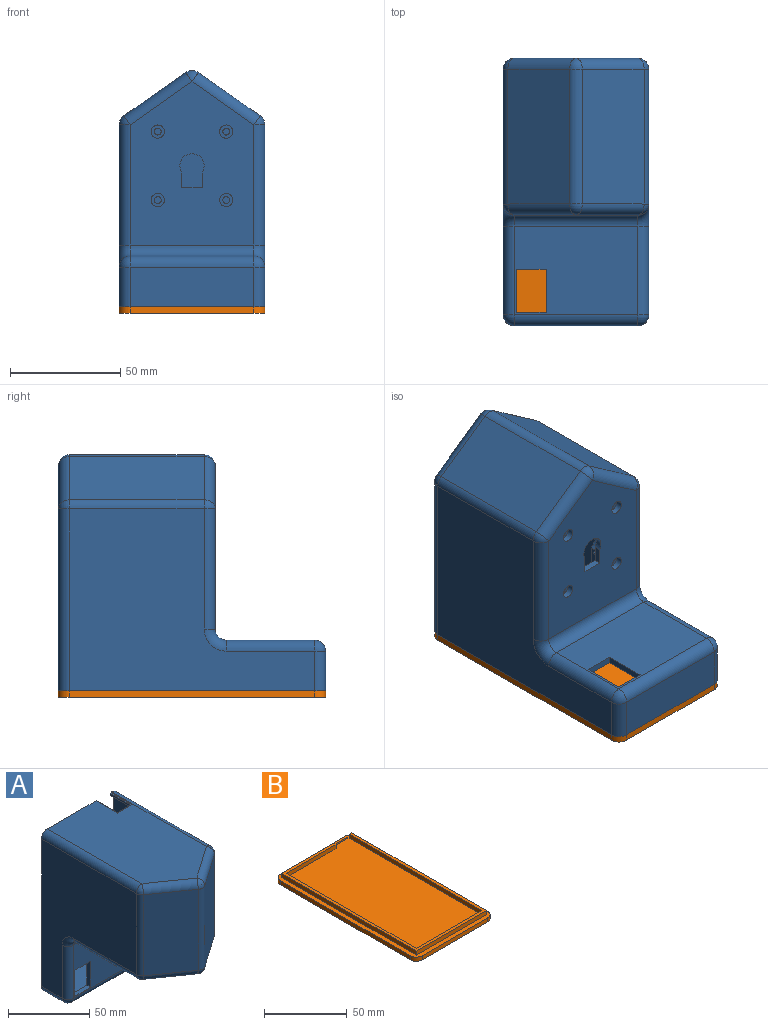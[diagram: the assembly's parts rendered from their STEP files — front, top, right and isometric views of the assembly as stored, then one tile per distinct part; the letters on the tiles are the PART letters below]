
ASSEMBLY  parts=2 mates=1
PART A: 93 faces, bbox 66x107x121 mm
  f0: plane 102x56mm, normal (0,0,1), area 4913.5mm2, adj f1,f3,f17,f56,f57,f63,f64
  f1: plane 13.5x0.75mm, normal (0,1,0), area 10.1mm2, adj f0,f3,f5,f90
  f2: plane 17.5x1.5mm, normal (-1,0,0), area 26.2mm2, adj f17,f89,f90,f92
  f3: plane 18.5x0.75mm, normal (1,0,0), area 13.9mm2, adj f0,f1,f17,f90
  f4: plane 18.5x0.75mm, normal (1,0,0), area 13.9mm2, adj f10,f17,f37,f89
  f5: plane 18.5x0.75mm, normal (-1,0,0), area 13.9mm2, adj f1,f17,f64,f90
  f6: plane 16.5x14.35mm, normal (0,0,1), area 236.8mm2, adj f18,f40,f43,f49
  f7: plane 38x23mm, normal (0,0,1), area 533.9mm2, adj f32,f39,f40,f41,f42,f43,f46,f47
  f8: plane 74x56mm, normal (0,0,-1), area 3336.8mm2, adj f22,f25,f28,f31,f32,f46,f47,f48
  f9: plane 86.01x60mm, normal (0,0,1), area 1780.7mm2, adj f14,f16,f18,f54,f55,f83,f84,f85
  f10: plane 106.01x60mm, normal (0,0,-1), area 5480.4mm2, adj f4,f14,f16,f17,f37,f38,f54,f55
  f11: plane 111x82.4mm, normal (-1,0,0), area 5947.7mm2, adj f17,f56,f60,f68,f69,f70,f74
  f12: plane 56x18mm, normal (0,0,-1), area 1008mm2, adj f17,f68,f76,f77
  f13: plane 111x82.4mm, normal (1,0,0), area 5947.7mm2, adj f17,f64,f72,f76,f79,f81,f82
  f14: plane 115x85mm, normal (-1,0,0), area 6395mm2, adj f9,f10,f15,f17,f18,f55
  f15: plane 60x20mm, normal (0,0,1), area 1200mm2, adj f14,f16,f17,f18
  f16: plane 115x85mm, normal (1,0,0), area 6395mm2, adj f9,f10,f15,f17,f18,f54
  f17: plane 121x66mm, normal (0,1,0), area 1027mm2, adj f0,f2,f3,f4,f5,f10,f11,f12
  f18: plane 60x52mm, normal (0,1,0), area 2823.8mm2, adj f6,f9,f14,f15,f16,f33,f34,f35
  f19: plane 56x40mm, normal (0,-1,0), area 1976.7mm2, adj f33,f34,f35,f36,f69,f77,f78,f82
  f20: cylinder r=1.55mm len=6mm, axis (0,0,-1), area 58.4mm2, adj f21,f86
  f21: plane 6x6mm, normal (0,0,-1), area 20.7mm2, adj f20,f22
  f22: cylinder r=3mm len=6mm, axis (0,0,-1), area 56.5mm2, adj f8,f21
  f23: cylinder r=1.55mm len=6mm, axis (0,0,-1), area 58.4mm2, adj f24,f86
  f24: plane 6x6mm, normal (0,0,-1), area 20.7mm2, adj f23,f25
  f25: cylinder r=3mm len=6mm, axis (0,0,-1), area 56.5mm2, adj f8,f24
  f26: cylinder r=1.55mm len=6mm, axis (0,0,-1), area 58.4mm2, adj f27,f86
  f27: plane 6x6mm, normal (0,0,-1), area 20.7mm2, adj f26,f28
  f28: cylinder r=3mm len=6mm, axis (0,0,-1), area 56.5mm2, adj f8,f27
  f29: cylinder r=1.55mm len=6mm, axis (0,0,-1), area 58.4mm2, adj f30,f86
  f30: plane 6x6mm, normal (0,0,-1), area 20.7mm2, adj f29,f31
  f31: cylinder r=3mm len=6mm, axis (0,0,-1), area 56.5mm2, adj f8,f30
  f32: cylinder r=5.5mm len=11mm, axis (0,0,-1), area 69.3mm2, adj f7,f8,f46,f48
  f33: plane 19.5x3mm, normal (1,0,0), area 58.5mm2, adj f18,f19,f34,f36
  f34: plane 13.5x3mm, normal (0,0,1), area 40.5mm2, adj f18,f19,f33,f35
  f35: plane 19.5x3mm, normal (-1,0,0), area 58.5mm2, adj f18,f19,f34,f36
  f36: plane 13.5x3mm, normal (0,0,-1), area 40.5mm2, adj f18,f19,f33,f35
  f37: plane 13.5x0.75mm, normal (0,1,0), area 10.1mm2, adj f4,f10,f38,f89
  f38: plane 18.5x0.75mm, normal (-1,0,0), area 13.9mm2, adj f10,f17,f37,f89
  f39: cylinder r=11.5mm len=23mm, axis (0,0,1), area 323.1mm2, adj f7,f40,f43,f86
  f40: plane 35.84x8mm, normal (-1,0,0), area 175.6mm2, adj f6,f7,f18,f39,f49,f50,f51,f86
  f41: cylinder r=0.5mm len=2mm, axis (0,0,1), area 6.3mm2, adj f7,f44
  f42: cylinder r=0.5mm len=2mm, axis (0,0,1), area 6.3mm2, adj f7,f45
  f43: plane 35.84x8mm, normal (1,0,0), area 175.6mm2, adj f6,f7,f18,f39,f49,f50,f51,f86
  f44: plane 1x1mm, normal (0,0,1), area 0.8mm2, adj f41
  f45: plane 1x1mm, normal (0,0,1), area 0.8mm2, adj f42
  f46: plane 7.23x3mm, normal (-1,0,0), area 21.7mm2, adj f7,f8,f32,f47
  f47: plane 9.5x3mm, normal (0,-1,0), area 28.5mm2, adj f7,f8,f46,f48
  f48: plane 7.23x3mm, normal (1,0,0), area 21.7mm2, adj f7,f8,f32,f47
  f49: plane 16.5x2mm, normal (0,-1,0), area 33mm2, adj f6,f40,f43,f51
  f50: plane 16.5x2mm, normal (0,1,0), area 33mm2, adj f7,f40,f43,f51
  f51: plane 16.5x3mm, normal (0,0,1), area 49.5mm2, adj f40,f43,f49,f50
  f52: plane 61x28mm, normal (0.57,-0.82,0), area 2085.1mm2, adj f62,f63,f71,f72
  f53: plane 61x28mm, normal (-0.57,-0.82,0), area 2085.1mm2, adj f57,f60,f61,f62
  f54: plane 63x30mm, normal (0.57,0.82,0), area 2307.3mm2, adj f9,f10,f16,f55
  f55: plane 63x30mm, normal (-0.57,0.82,0), area 2307.3mm2, adj f9,f10,f14,f54
  f56: cylinder r=5mm len=82.4mm, axis (0,1,0), area 647.1mm2, adj f0,f11,f17,f58
  f57: cylinder r=5mm len=30.87mm, axis (0.82,-0.57,0), area 268.5mm2, adj f0,f53,f58,f59
  f58: sphere r=5mm, area 24mm2, adj f56,f57,f60
  f59: sphere r=5mm, area 30.5mm2, adj f57,f62,f63
  f60: cylinder r=5mm len=61mm, axis (0,0,1), area 292.8mm2, adj f11,f53,f58,f65
  f61: cylinder r=5mm len=30.87mm, axis (0.82,-0.57,0), area 268.5mm2, adj f8,f53,f65,f66
  f62: cylinder r=5mm len=61mm, axis (0,0,1), area 372.6mm2, adj f52,f53,f59,f66
  f63: cylinder r=5mm len=30.87mm, axis (-0.82,-0.57,0), area 268.5mm2, adj f0,f52,f59,f67
  f64: cylinder r=5mm len=82.4mm, axis (0,1,0), area 647.1mm2, adj f0,f5,f13,f17,f67
  f65: sphere r=5mm, area 24mm2, adj f60,f61,f70
  f66: sphere r=5mm, area 30.5mm2, adj f61,f62,f71
  f67: sphere r=5mm, area 24mm2, adj f63,f64,f72
  f68: cylinder r=5mm len=18mm, axis (0,1,0), area 141.4mm2, adj f11,f12,f17,f73
  f69: cylinder r=5mm len=40mm, axis (0,0,1), area 314.2mm2, adj f11,f19,f73,f74
  f70: cylinder r=5mm len=54.4mm, axis (0,1,0), area 427.2mm2, adj f8,f11,f65,f74
  f71: cylinder r=5mm len=30.87mm, axis (0.82,0.57,0), area 268.5mm2, adj f8,f52,f66,f75
  f72: cylinder r=5mm len=61mm, axis (0,0,1), area 292.8mm2, adj f13,f52,f67,f75
  f73: sphere r=5mm, area 39.3mm2, adj f68,f69,f77
  f74: torus R=10mm, axis (1,0,0), area 84.1mm2, adj f11,f69,f70,f78
  f75: sphere r=5mm, area 24mm2, adj f71,f72,f79
  f76: cylinder r=5mm len=18mm, axis (0,1,0), area 141.4mm2, adj f12,f13,f17,f80
  f77: cylinder r=5mm len=56mm, axis (-1,0,0), area 439.8mm2, adj f12,f19,f73,f80
  f78: cylinder r=5mm len=56mm, axis (1,0,0), area 439.8mm2, adj f8,f19,f74,f81
  f79: cylinder r=5mm len=54.4mm, axis (0,1,0), area 427.2mm2, adj f8,f13,f75,f81
  f80: sphere r=5mm, area 39.3mm2, adj f76,f77,f82
  f81: torus R=10mm, axis (-1,0,0), area 84.1mm2, adj f13,f78,f79,f82
  f82: cylinder r=5mm len=40mm, axis (0,0,-1), area 314.2mm2, adj f13,f19,f80,f81
  f83: plane 65x4mm, normal (-1,0,0), area 214.6mm2, adj f9,f84,f86,f88
  f84: plane 42.3x4mm, normal (0,-1,0), area 169.2mm2, adj f9,f83,f85,f86
  f85: plane 65x4mm, normal (1,0,0), area 214.6mm2, adj f9,f84,f86,f87
  f86: plane 42.3x42.3mm, normal (0,0,1), area 1166.6mm2, adj f20,f23,f26,f29,f39,f40,f43,f83
  f87: plane 22.7x12.9mm, normal (0,0.17,0.98), area 297.3mm2, adj f18,f40,f85,f86
  f88: plane 22.7x12.9mm, normal (0,0.17,0.98), area 297.3mm2, adj f18,f43,f83,f86
  f89: plane 18.5x13.5mm, normal (0,0,-1), area 48.5mm2, adj f2,f4,f17,f37,f38,f91,f92
  f90: plane 18.5x13.5mm, normal (0,0,1), area 48.5mm2, adj f1,f2,f3,f5,f17,f91,f92
  f91: plane 17.5x1.5mm, normal (1,0,0), area 26.2mm2, adj f17,f89,f90,f92
  f92: plane 11.5x1.5mm, normal (0,1,0), area 17.2mm2, adj f2,f89,f90,f91
PART B: 26 faces, bbox 66x121x6 mm
  f0: plane 115x3mm, normal (1,0,0), area 345mm2, adj f1,f9,f10,f15
  f1: plane 3x2mm, normal (0,1,0), area 6mm2, adj f0,f2,f10,f15
  f2: plane 113x3mm, normal (-1,0,0), area 339mm2, adj f1,f3,f10,f15
  f3: plane 56x3mm, normal (0,1,0), area 168mm2, adj f2,f4,f10,f15
  f4: plane 111x3mm, normal (1,0,0), area 333mm2, adj f3,f5,f10,f15
  f5: plane 42.5x3mm, normal (0,-1,0), area 127.5mm2, adj f4,f6,f10,f15
  f6: plane 3x2mm, normal (1,0,0), area 6mm2, adj f5,f7,f10,f15
  f7: plane 44.5x3mm, normal (0,1,0), area 133.5mm2, adj f6,f8,f10,f15
  f8: plane 115x3mm, normal (-1,0,0), area 345mm2, adj f7,f9,f10,f15
  f9: plane 60x3mm, normal (0,-1,0), area 180mm2, adj f0,f8,f10,f15
  f10: plane 115x60mm, normal (0,0,1), area 657mm2, adj f0,f1,f2,f3,f4,f5,f6,f7
  f11: plane 56x3mm, normal (0,1,0), area 168mm2, adj f15,f16,f17,f20
  f12: plane 111x3mm, normal (-1,0,0), area 333mm2, adj f15,f16,f17,f18
  f13: plane 56x3mm, normal (0,-1,0), area 168mm2, adj f15,f16,f18,f19
  f14: plane 111x3mm, normal (1,0,0), area 333mm2, adj f15,f16,f19,f20
  f15: plane 121x66mm, normal (0,0,1), area 7290.3mm2, adj f0,f1,f2,f3,f4,f5,f6,f7
  f16: plane 121x66mm, normal (0,0,-1), area 7964.5mm2, adj f11,f12,f13,f14,f17,f18,f19,f20
  f17: cylinder r=5mm len=5mm, axis (0,0,-1), area 23.6mm2, adj f11,f12,f15,f16
  f18: cylinder r=5mm len=5mm, axis (0,0,-1), area 23.6mm2, adj f12,f13,f15,f16
  f19: cylinder r=5mm len=5mm, axis (0,0,-1), area 23.6mm2, adj f13,f14,f15,f16
  f20: cylinder r=5mm len=5mm, axis (0,0,-1), area 23.6mm2, adj f11,f14,f15,f16
  f21: plane 11.5x1.5mm, normal (0,0,1), area 17.2mm2, adj f22,f23,f24,f25
  f22: plane 1.5x1mm, normal (-1,0,0), area 1.5mm2, adj f15,f21,f23,f25
  f23: plane 11.5x1mm, normal (0,-1,0), area 11.5mm2, adj f15,f21,f22,f24
  f24: plane 1.5x1mm, normal (1,0,0), area 1.5mm2, adj f15,f21,f23,f25
  f25: plane 11.5x1mm, normal (0,1,0), area 11.5mm2, adj f15,f21,f22,f24
PLACE A rot(axis=(-1,0,0),90deg) t=(0,-60.73,-20.64)mm
PLACE B t=(0,-60.73,-23.64)mm
MATE fastened B.f15 <-> A.f17  axis (0,0,1) through (30,-3.23,-20.64)mm
